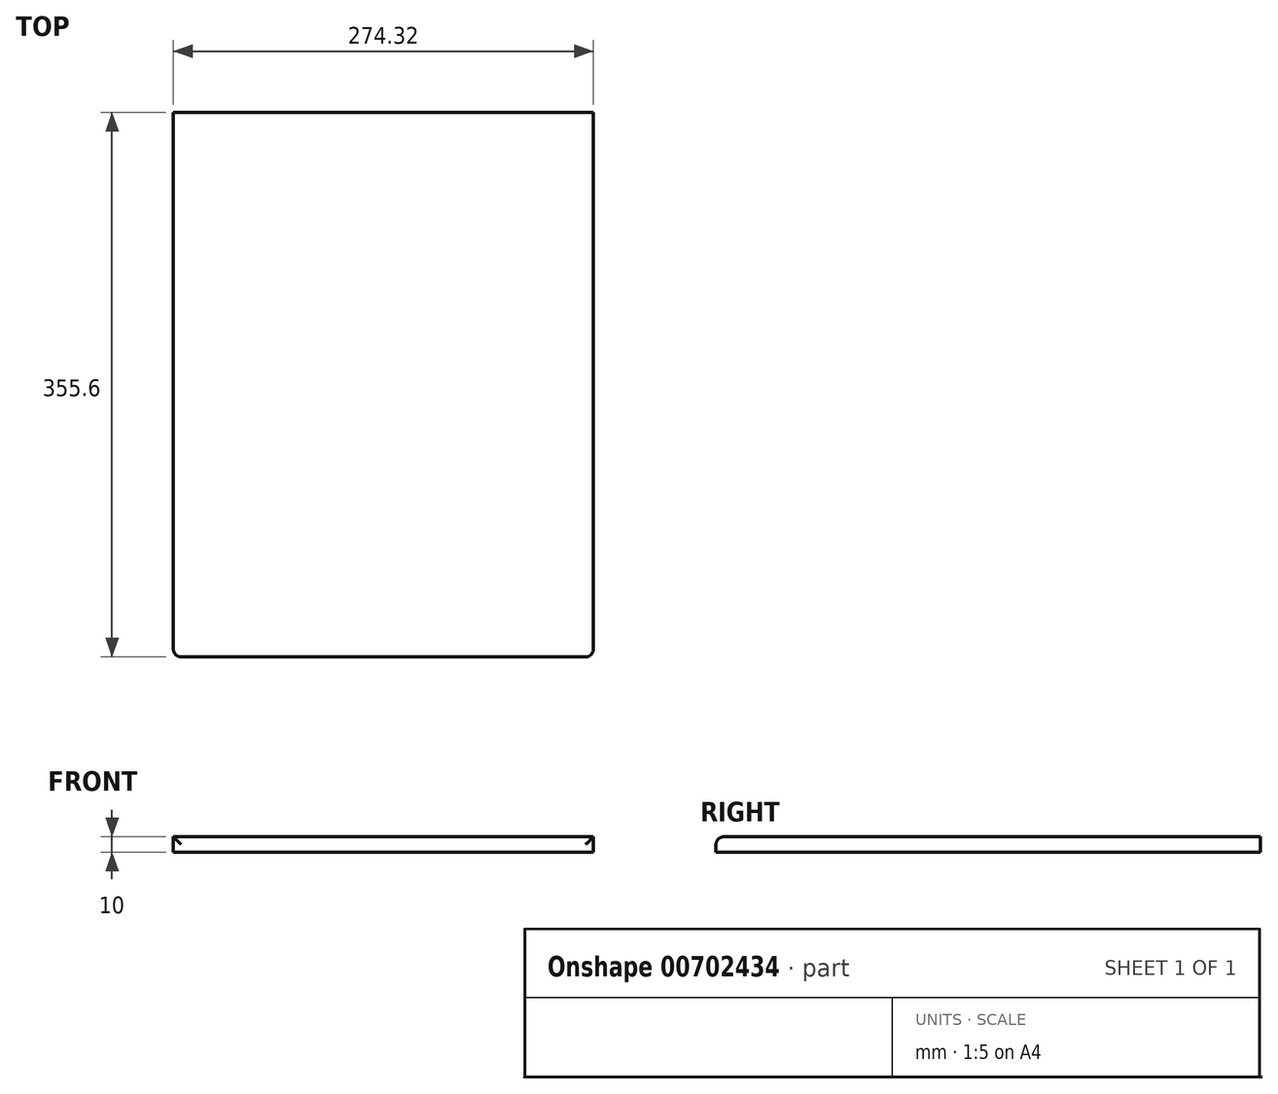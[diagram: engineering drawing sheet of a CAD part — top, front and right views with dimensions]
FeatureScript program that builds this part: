
annotation { "Feature Type Name" : "Feature", "Feature Type Description" : "" }
export const myFeature = defineFeature(function(context is Context, id is Id, definition is map)
    precondition{}
    {
        {
            var Q0;
            Q0=qCreatedBy(makeId("Top.planeOp"),FACE);
            var sketch = newSketch(context, id + "F0", { "sketchPlane" : qUnion([Q0])});
            skLineSegment(sketch, "E0.bottom", {"start": v(-137.16, 170.86) * mm, "end": v(137.16, 170.86) * mm});
            skLineSegment(sketch, "E0.top", {"start": v(-137.16, -184.74) * mm, "end": v(137.16, -184.74) * mm});
            skLineSegment(sketch, "E0.left", {"start": v(-137.16, 170.86) * mm, "end": v(-137.16, -184.74) * mm});
            skLineSegment(sketch, "E0.right", {"start": v(137.16, 170.86) * mm, "end": v(137.16, -184.74) * mm});
            skPoint(sketch, "E0.middle", {"position": v(0, -6.94) * mm});
            skSolve(sketch);
        }
        {
            var Q0;
            Q0 = qSketchRegion(id + "F0", true);
            extrude(context, id + "F1", {"entities" : qUnion([Q0]), "depth" : 10 * mm, "offsetDistance" : 25.4 * mm});
        }
        {
            var Q0;
            Q0=makeQuery(id+"F1.opExtrude","SWEPT_EDGE",EDGE,{"disambiguationData":[OSD([sQuery(id+"F0.wireOp",EDGE,"E0.top"),sQuery(id+"F0.wireOp",EDGE,"E0.right")])]});
            var Q1;
            Q1=makeQuery(id+"F1.opExtrude","SWEPT_EDGE",EDGE,{"disambiguationData":[OSD([sQuery(id+"F0.wireOp",EDGE,"E0.top"),sQuery(id+"F0.wireOp",EDGE,"E0.left")])]});
            var Q2;
            Q2=makeQuery(id+"F1.opExtrude","CAP_EDGE",EDGE,{"disambiguationData":[OSD([sQuery(id+"F0.wireOp",EDGE,"E0.top")])],"isStart":false});
            fillet(context, id + "F2", {"entities" : qUnion([Q0, Q1, Q2]), "radius" : 5.08 * mm, "tangentPropagation" : true, "allowEdgeOverflow" : false});
        }
    });
